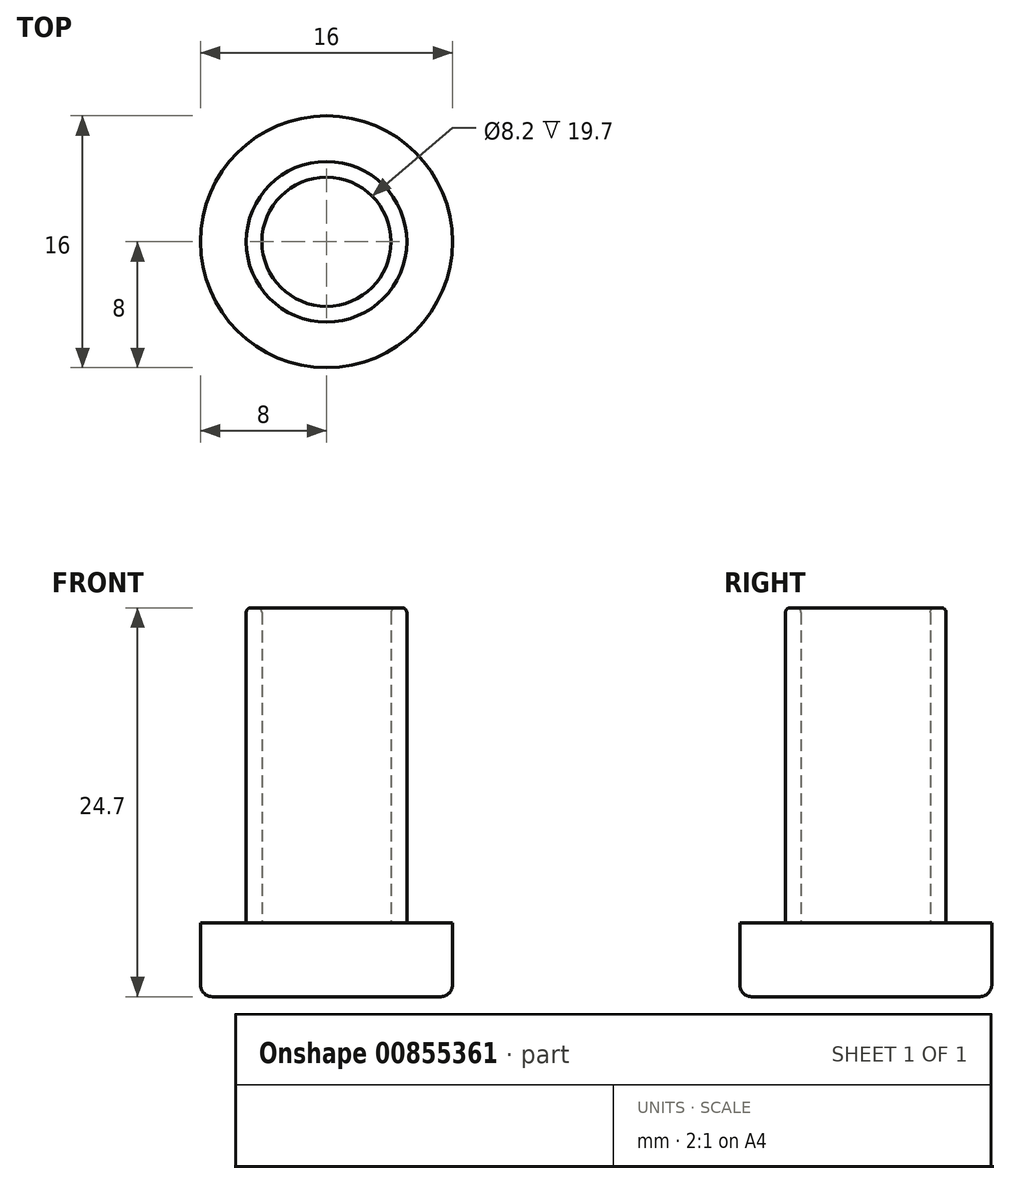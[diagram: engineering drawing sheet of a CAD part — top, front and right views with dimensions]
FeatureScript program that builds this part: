
annotation { "Feature Type Name" : "Feature", "Feature Type Description" : "" }
export const myFeature = defineFeature(function(context is Context, id is Id, definition is map)
    precondition{}
    {
        {
            var Q0;
            Q0=qCreatedBy(makeId("Top.planeOp"),FACE);
            var sketch = newSketch(context, id + "F0", { "sketchPlane" : qUnion([Q0])});
            skCircle(sketch, "E0", {"center": v(0, 0) * mm, "radius": 8 * mm});
            skCircle(sketch, "E1", {"center": v(0, 0) * mm, "radius": 5.1 * mm});
            skCircle(sketch, "E2", {"center": v(0, 0) * mm, "radius": 4.1 * mm});
            skSolve(sketch);
        }
        {
            var Q0;
            Q0 = qSketchRegion(id + "F0", true);
            var Q1;
            Q1=makeQuery(id+"F0.imprint","IMPRINT",FACE,{"disambiguationData":[TD([[makeQuery(id+"F0.imprint","IMPRINT",EDGE,{"derivedFrom":sQuery(id+"F0.wireOp",EDGE,"E1")}),1.0]])]});
            var Q2;
            Q2=makeQuery(id+"F0.imprint","IMPRINT",FACE,{"disambiguationData":[TD([[makeQuery(id+"F0.imprint","IMPRINT",EDGE,{"derivedFrom":sQuery(id+"F0.wireOp",EDGE,"E2")}),1.0]])]});
            extrude(context, id + "F1", {"entities" : qUnion([Q0, Q1, Q2]), "depth" : 4.7 * mm, "offsetDistance" : 25.4 * mm});
        }
        {
            var Q0;
            Q0=makeQuery(id+"F0.imprint","IMPRINT",FACE,{"disambiguationData":[TD([[makeQuery(id+"F0.imprint","IMPRINT",EDGE,{"derivedFrom":sQuery(id+"F0.wireOp",EDGE,"E1")}),1.0]])]});
            extrude(context, id + "F2", {"entities" : qUnion([Q0]), "operationType" : NewBodyOperationType.ADD, "depth" : 24.7 * mm, "offsetDistance" : 25.4 * mm});
        }
        {
            var Q0;
            Q0=makeQuery(id+"F2.opExtrude","CAP_EDGE",EDGE,{"disambiguationData":[OSD([sQuery(id+"F0.wireOp",EDGE,"E1")])],"isStart":false});
            var Q1;
            Q1=makeQuery(id+"F2.opExtrude","CAP_EDGE",EDGE,{"disambiguationData":[OSD([sQuery(id+"F0.wireOp",EDGE,"E2")])],"isStart":false});
            fillet(context, id + "F3", {"entities" : qUnion([Q0, Q1]), "radius" : .3 * mm, "tangentPropagation" : true, "allowEdgeOverflow" : false});
        }
        {
            var Q0;
            Q0=makeQuery(id+"F1.opExtrude","CAP_EDGE",EDGE,{"disambiguationData":[OSD([sQuery(id+"F0.wireOp",EDGE,"E0")])],"isStart":true});
            fillet(context, id + "F4", {"entities" : qUnion([Q0]), "radius" : .75 * mm, "tangentPropagation" : true, "allowEdgeOverflow" : false});
        }
    });
